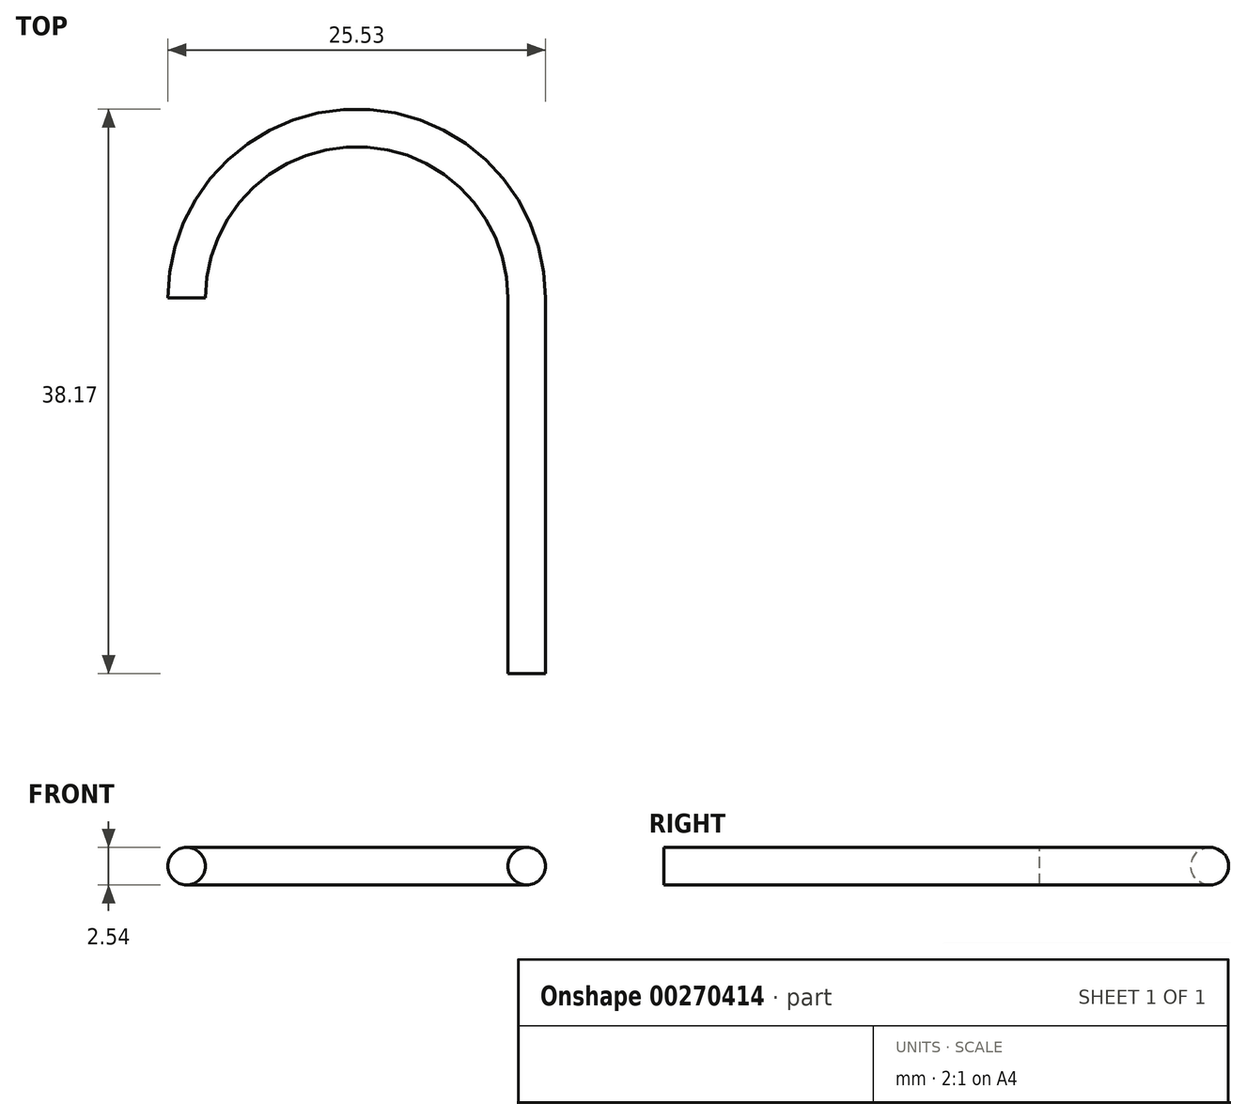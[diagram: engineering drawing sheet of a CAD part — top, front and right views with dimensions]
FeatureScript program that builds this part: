
annotation { "Feature Type Name" : "Feature", "Feature Type Description" : "" }
export const myFeature = defineFeature(function(context is Context, id is Id, definition is map)
    precondition{}
    {
        {
            var Q0;
            Q0=qCreatedBy(makeId("Top.planeOp"),FACE);
            var sketch = newSketch(context, id + "F0", { "sketchPlane" : qUnion([Q0])});
            skLineSegment(sketch, "E0", {"start": v(0, 0) * mm, "end": v(0, 25.4) * mm});
            skArc(sketch, "E1", {"start": v(0, 25.4) * mm, "mid": v(-11.5, 36.9) * mm, "end": v(-23, 25.4) * mm});
            skSolve(sketch);
        }
        {
            var Q0;
            Q0=qCreatedBy(makeId("Front.planeOp"),FACE);
            var sketch = newSketch(context, id + "F1", { "sketchPlane" : qUnion([Q0])});
            skCircle(sketch, "E2", {"center": v(0, 0) * mm, "radius": 1.27 * mm});
            skSolve(sketch);
        }
        {
            var Q0;
            Q0=makeQuery(id+"F1.imprint","IMPRINT",FACE,{"disambiguationData":[TD([[makeQuery(id+"F1.imprint","IMPRINT",EDGE,{"derivedFrom":sQuery(id+"F1.wireOp",EDGE,"E2")}),1.0]])]});
            var Q1;
            Q1=sQuery(id+"F0.wireOp",EDGE,"E0");
            var Q2;
            Q2=sQuery(id+"F0.wireOp",EDGE,"E1");
            sweep(context, id + "F2", {"profiles" : qUnion([Q0]), "path" : qUnion([Q1, Q2])});
        }
    });
